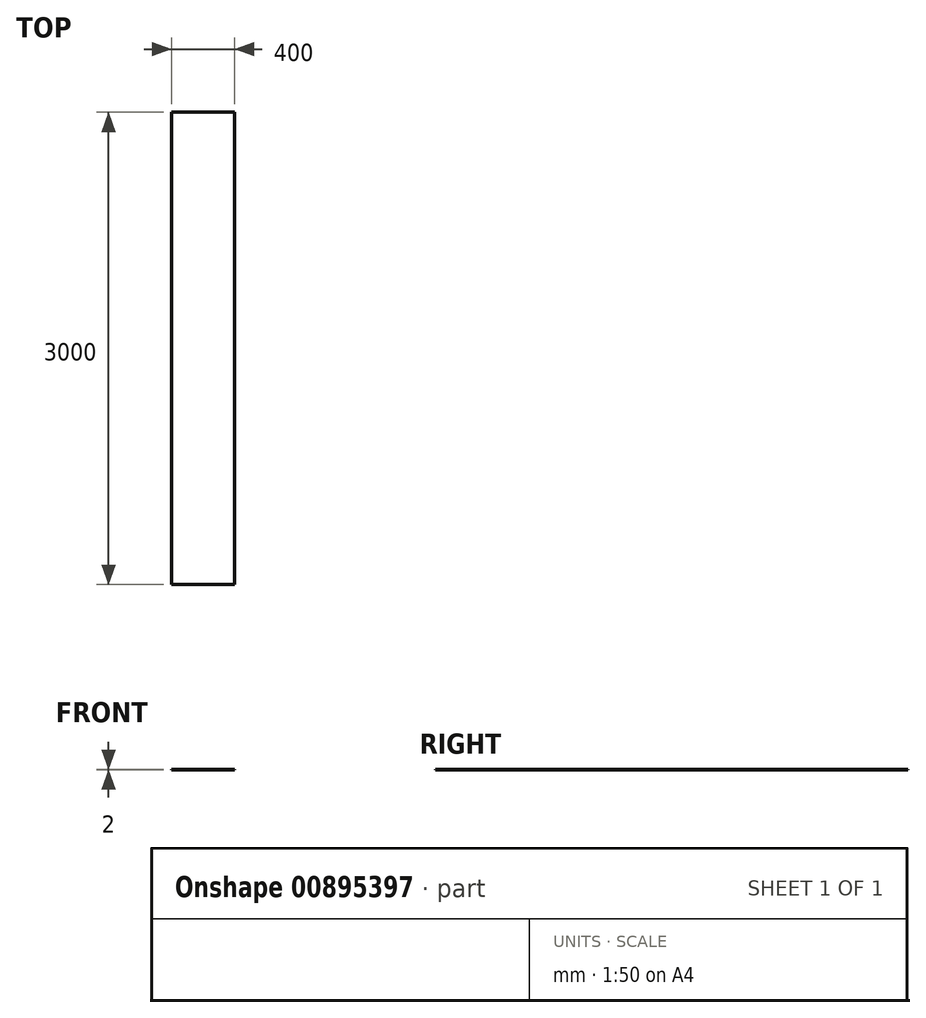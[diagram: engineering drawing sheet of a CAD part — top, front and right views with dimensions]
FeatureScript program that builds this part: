
annotation { "Feature Type Name" : "Feature", "Feature Type Description" : "" }
export const myFeature = defineFeature(function(context is Context, id is Id, definition is map)
    precondition{}
    {
        {
            var Q0;
            Q0=qCreatedBy(makeId("Top.planeOp"),FACE);
            var sketch = newSketch(context, id + "F0", { "sketchPlane" : qUnion([Q0])});
            skLineSegment(sketch, "E0.bottom", {"start": v(200, 1500) * mm, "end": v(-200, 1500) * mm});
            skLineSegment(sketch, "E0.top", {"start": v(200, -1500) * mm, "end": v(-200, -1500) * mm});
            skLineSegment(sketch, "E0.left", {"start": v(200, 1500) * mm, "end": v(200, -1500) * mm});
            skLineSegment(sketch, "E0.right", {"start": v(-200, 1500) * mm, "end": v(-200, -1500) * mm});
            skPoint(sketch, "E0.middle", {"position": v(0, 0) * mm});
            skSolve(sketch);
        }
        {
            var Q0;
            Q0=makeQuery(id+"F0.imprint","IMPRINT",FACE,{"disambiguationData":[TD([[makeQuery(id+"F0.imprint","IMPRINT",EDGE,{"derivedFrom":sQuery(id+"F0.wireOp",EDGE,"E0.bottom")}),1.0]])]});
            extrude(context, id + "F1", {"entities" : qUnion([Q0]), "depth" : 2 * mm, "offsetDistance" : 25 * mm});
        }
    });
